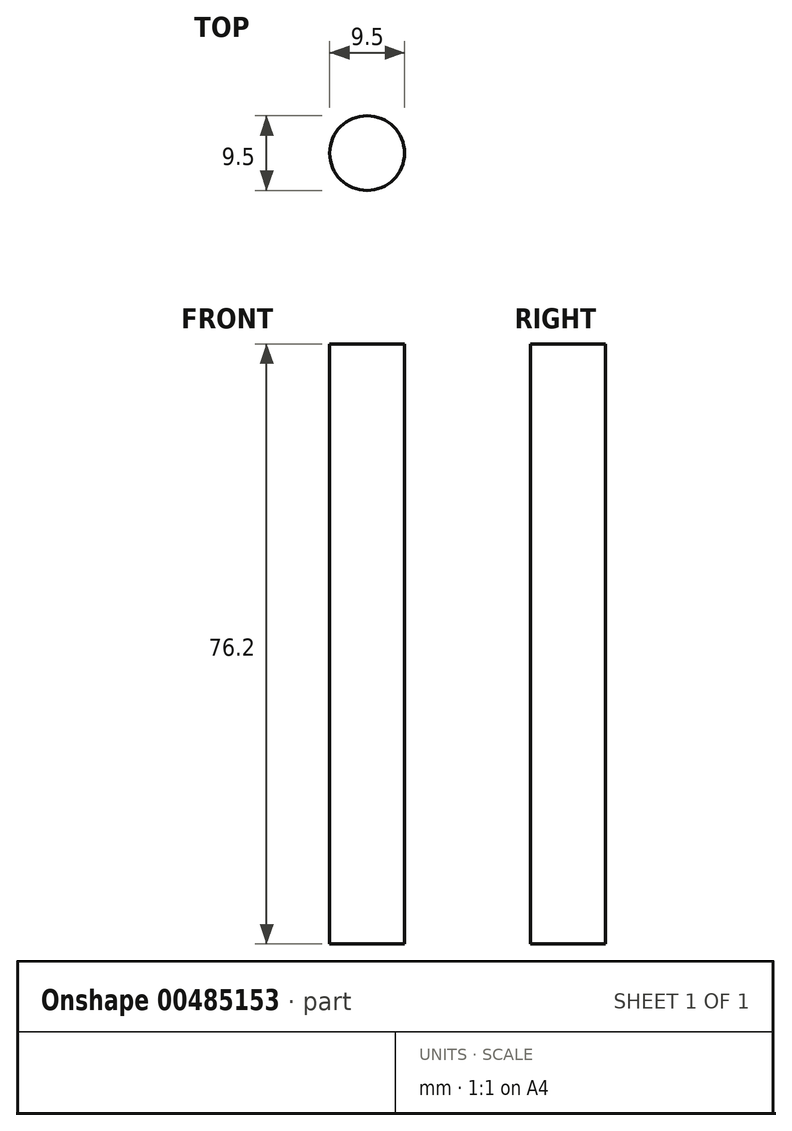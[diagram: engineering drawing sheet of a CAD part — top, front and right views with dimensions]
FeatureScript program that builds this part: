
annotation { "Feature Type Name" : "Feature", "Feature Type Description" : "" }
export const myFeature = defineFeature(function(context is Context, id is Id, definition is map)
    precondition{}
    {
        {
            var Q0;
            Q0=qCreatedBy(makeId("Top.planeOp"),FACE);
            var sketch = newSketch(context, id + "F0", { "sketchPlane" : qUnion([Q0])});
            skCircle(sketch, "E0", {"center": v(0, 0) * mm, "radius": 4.75 * mm});
            skSolve(sketch);
        }
        {
            var Q0;
            Q0 = qSketchRegion(id + "F0", true);
            extrude(context, id + "F1", {"entities" : qUnion([Q0]), "depth" : 76.2 * mm});
        }
    });
